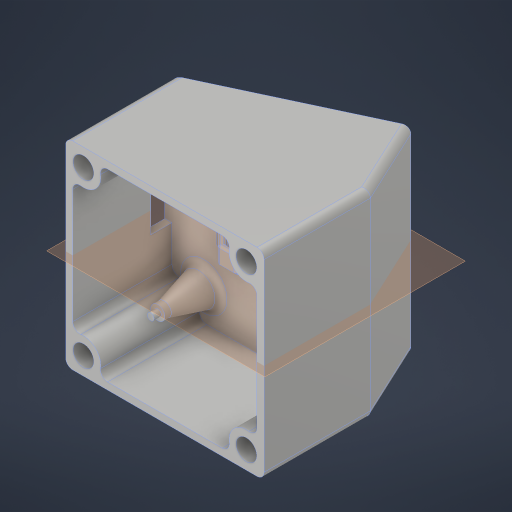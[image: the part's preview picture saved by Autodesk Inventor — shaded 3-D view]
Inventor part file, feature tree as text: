
AUTODESK INVENTOR PART (.ipt)
format: ipt  version: 2023 (Build 270158000, 158)  size: 464,896 bytes
history: native  units: in
note: dims shown in document units (in); Inventor stores cm internally (conversion verified against a paired STEP export)
features: sketch x8, extrude x8, projected_geometry x4, fillet x2, chamfer x2, hole x1, mirror x1, shell x1, plane x1
ambient origin geometry x8: Origin, YZ Plane, XZ Plane, XY Plane, X Axis, Y Axis, Z Axis, Center Point
bodies: Solid1 (feature_tree)
feature tree (28):
  sketch  "Sketch1"  dims[d0=1.4961in d1=1.4961in]
  extrude  "Extrusion1"  Depth=1.4961in
  hole  "Hole1"  [1 undecoded]
  extrude  "Extrusion6"  Depth=0.0787in
  mirror  "Mirror1"
  shell  "Shell1"  Thickness=0.3937in
  extrude  "Extrusion7"  Depth=0.0787in
  fillet  "Fillet1"  Radius=0.1575in
  extrude  "Extrusion2"  Depth=0.1575in
  chamfer  "Chamfer1"  Distance=0.5906in
  extrude  "Extrusion3"  Depth=0.315in
  sketch  "Sketch3"  dims[d5=1.1811in d6=0.0in d7=0.0787in d8=0.3937in]
  extrude  "Extrusion4"  Depth=0.315in
  plane  "Work Plane1"
  extrude  "Extrusion5"  Depth=0.315in
  chamfer  "Chamfer2"  Distance=0.0748in
  fillet  "Fillet3"  Radius=0.0787in
  extrude  "Extrusion8"  Depth=0.315in
  sketch  "Sketch2"  dims[d2=1.3386in d3=1.3386in]
  projected_geometry  "Projected Loop1"
  projected_geometry  "Projected Loop2"
  projected_geometry  "Projected Loop3"
  sketch  "Sketch4"  dims[d9=1.811in]
  sketch  "Sketch5"  dims[d10=0.2283in d11=0.2362in d12=0.385in d13=0.0787in d14=0.5635in d15=0.315in d16=0.8108in d17=0.0787in d18=0.1575in]
  sketch  "Sketch6"  dims[d19=0.1575in d20=0.1575in]
  sketch  "Sketch9"  dims[d21=0.1575in d22=0.5906in d23=0.0in]
  sketch  "Sketch10"  dims[d24=0.1181in d25=0.0787in d26=75.0deg d27=0.0748in d28=0.0748in d29=0.0748in d30=0.0748in d31=0.0787in d32=0.0in d33=0.4724in d34=0.2362in d35=0.0787in d36=1.1811in d37=0.0in d42=0.1969in d43=0.0in d44=0.0197in d45=0.0787in d46=0.481in d47=0.2283in d48=0.2283in d49=0.1969in d50=1.0in d51=0.2756in d52=0.0in d61=0.0787in d62=0.1718in d63=0.3937in d64=0.0in d65=0.0591in d66=0.1969in d67=0.5906in d68=45.0deg d69=45.0deg d70=0.5906in d71=0.1843in d72=0.0591in d73=0.0591in d74=1.5748in d75=1.5748in d76=0.2283in d77=0.2283in d80=0.315in d81=0.0in d82=0.2283in d60=0.0in]
  projected_geometry  "Project Cut Edges1"
note: 1 required parameter value undecoded (feature->parameter linkage not recoverable at this tier; creation-order binding heuristic only, values carry confidence <= 0.55)
